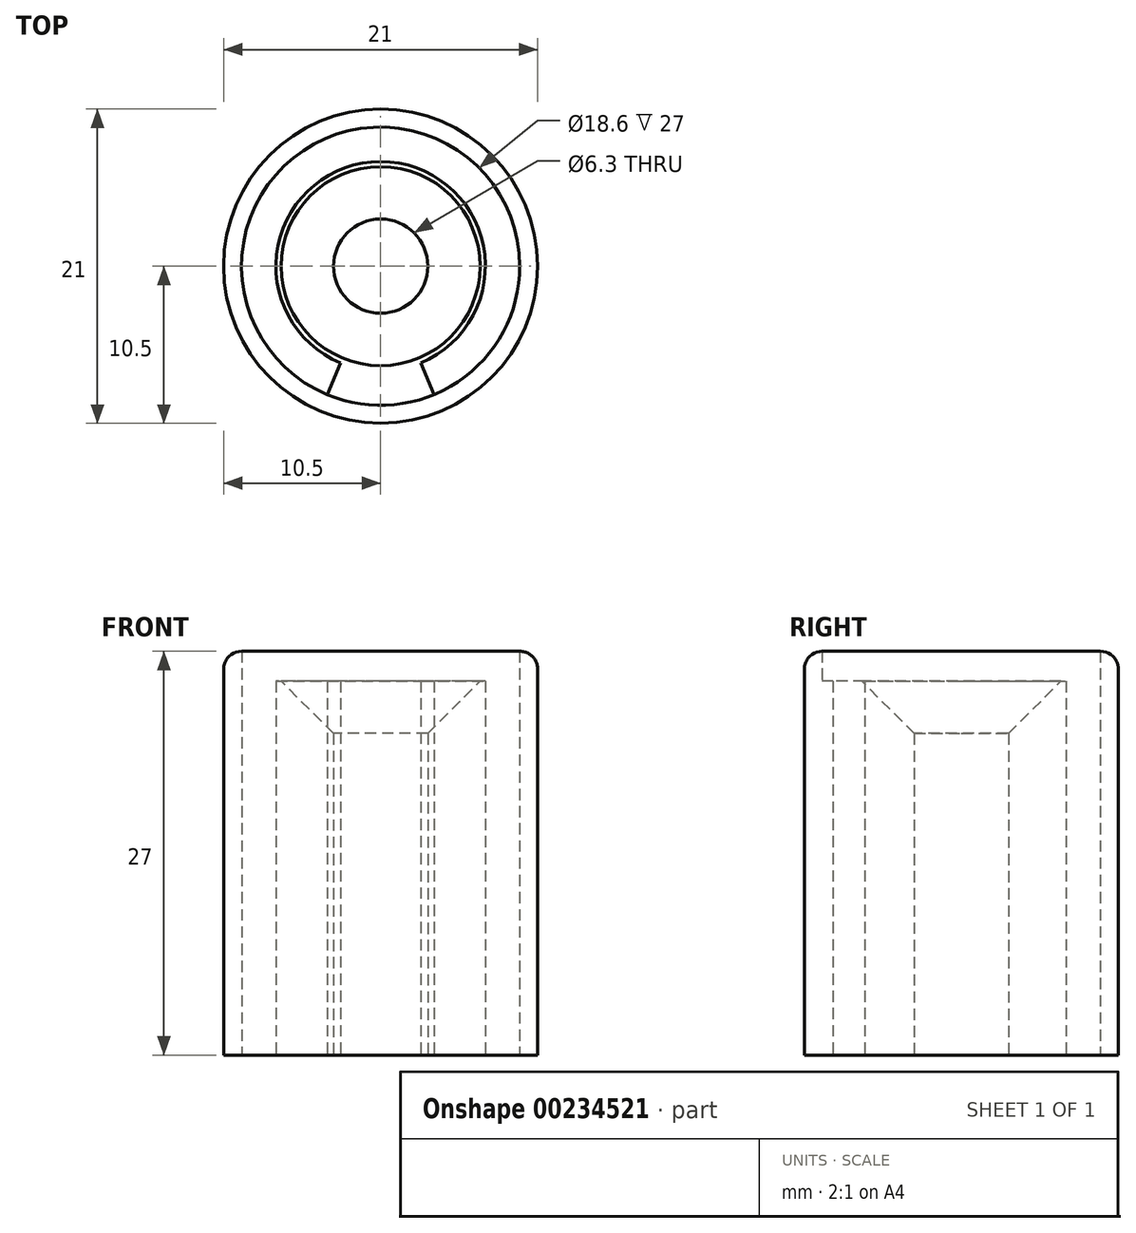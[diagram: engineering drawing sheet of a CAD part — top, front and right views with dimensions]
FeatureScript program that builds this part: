
annotation { "Feature Type Name" : "Feature", "Feature Type Description" : "" }
export const myFeature = defineFeature(function(context is Context, id is Id, definition is map)
    precondition{}
    {
        {
            var Q0;
            Q0=qCreatedBy(makeId("Top.planeOp"),FACE);
            var sketch = newSketch(context, id + "F0", { "sketchPlane" : qUnion([Q0])});
            skCircle(sketch, "E0", {"center": v(0, 0) * mm, "radius": 3.15 * mm});
            skArc(sketch, "E1", {"start": v(-2.68, -6.47) * mm, "mid": v(0, 7) * mm, "end": v(2.68, -6.47) * mm});
            skArc(sketch, "E2", {"start": v(-3.56, -8.6) * mm, "mid": v(0, 9.3) * mm, "end": v(3.56, -8.6) * mm});
            skCircle(sketch, "E3", {"center": v(0, 0) * mm, "radius": 10.5 * mm});
            skLineSegment(sketch, "E4.trimOffspring", {"start": v(-2.68, -6.47) * mm, "end": v(-3.56, -8.6) * mm});
            skLineSegment(sketch, "E5.MirrorCS", {"start": v(2.68, -6.47) * mm, "end": v(3.56, -8.6) * mm});
            skSolve(sketch);
        }
        {
            var Q0;
            Q0 = qSketchRegion(id + "F0", true);
            extrude(context, id + "F1", {"entities" : qUnion([Q0]), "depth" : 25 * mm});
        }
        {
            var Q0;
            Q0=makeQuery(id+"F1.opExtrude","CAP_EDGE",EDGE,{"disambiguationData":[OSD([sQuery(id+"F0.wireOp",EDGE,"E0")])],"isStart":false});
            chamfer(context, id + "F2", {"entities" : qUnion([Q0]), "width" : 3.5 * mm, "tangentPropagation" : true});
        }
        {
            var Q0;
            Q0=makeQuery(id+"F1.opExtrude","CAP_FACE",FACE,{"disambiguationData":[OSD([sQuery(id+"F0.wireOp",EDGE,"E0"),sQuery(id+"F0.wireOp",EDGE,"E1"),sQuery(id+"F0.wireOp",EDGE,"E2"),sQuery(id+"F0.wireOp",EDGE,"E3"),sQuery(id+"F0.wireOp",EDGE,"E4.trimOffspring"),sQuery(id+"F0.wireOp",EDGE,"E5.MirrorCS")])],"isStart":false});
            var sketch = newSketch(context, id + "F3", { "sketchPlane" : qUnion([Q0])});
            skCircle(sketch, "E6.0", {"center": v(0, 0) * mm, "radius": 10.5 * mm});
            skCircle(sketch, "E7", {"center": v(0, 0) * mm, "radius": 9.3 * mm});
            skSolve(sketch);
        }
        {
            var Q0;
            Q0 = qSketchRegion(id + "F3", true);
            extrude(context, id + "F4", {"entities" : qUnion([Q0]), "operationType" : NewBodyOperationType.ADD, "depth" : 2 * mm});
        }
        {
            var Q0;
            Q0=makeQuery(id+"F4.opExtrude","CAP_EDGE",EDGE,{"disambiguationData":[OSD([sQuery(id+"F3.wireOp",EDGE,"E6.0")])],"isStart":false});
            fillet(context, id + "F5", {"entities" : qUnion([Q0]), "radius" : 1.2 * mm, "tangentPropagation" : true, "allowEdgeOverflow" : false});
        }
    });
